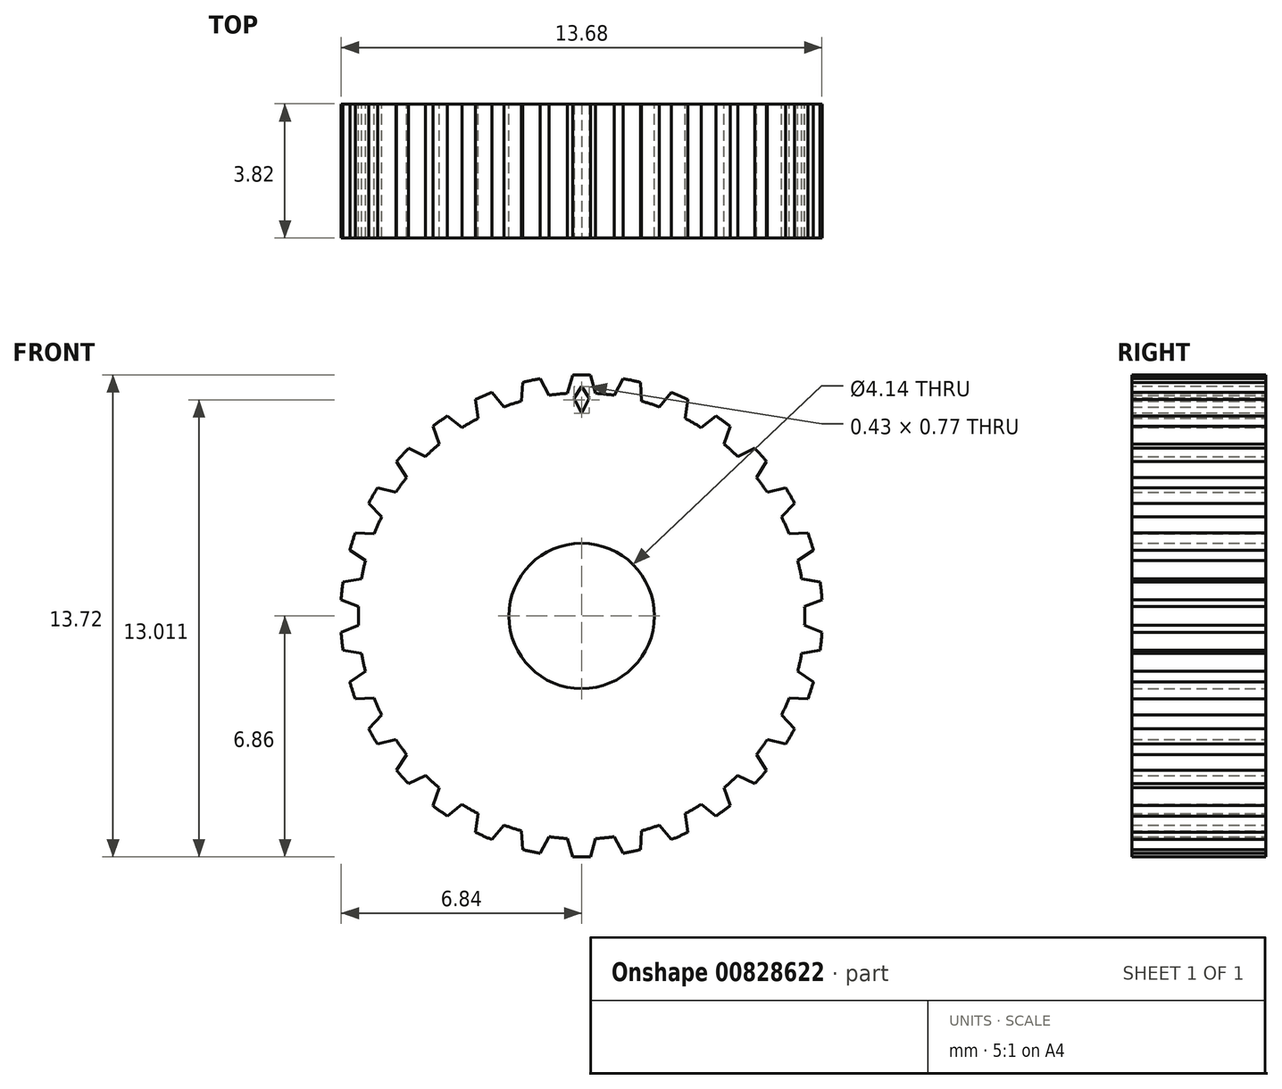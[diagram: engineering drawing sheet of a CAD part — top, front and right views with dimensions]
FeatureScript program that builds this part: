
annotation { "Feature Type Name" : "Feature", "Feature Type Description" : "" }
export const myFeature = defineFeature(function(context is Context, id is Id, definition is map)
    precondition{}
    {
        {
            var Q0;
            Q0=qCreatedBy(makeId("Front.planeOp"),FACE);
            var sketch = newSketch(context, id + "F0", { "sketchPlane" : qUnion([Q0])});
            skCircle(sketch, "E0", {"center": v(0, 0) * mm, "radius": 6.35 * mm});
            skCircle(sketch, "E1", {"center": v(0, 0) * mm, "radius": 6.86 * mm});
            skCircle(sketch, "E2", {"center": v(0, 0) * mm, "radius": 2.07 * mm});
            skLineSegment(sketch, "E3", {"start": v(-0.4, 6.34) * mm, "end": v(-0.25, 6.85) * mm});
            skLineSegment(sketch, "E4.MirrorCS", {"start": v(0.4, 6.34) * mm, "end": v(0.25, 6.85) * mm});
            skSolve(sketch);
        }
        {
            var Q0;
            {var subQ0=sQuery(id+"F0.wireOp",EDGE,"E3");Q0=makeQuery(id+"F0.imprint","IMPRINT",FACE,{"disambiguationData":[TD([[makeQuery(id+"F0.imprint","IMPRINT",EDGE,{"derivedFrom":subQ0}),-1.0]])]});}
            var Q1;
            Q1=makeQuery(id+"F0.imprint","IMPRINT",FACE,{"disambiguationData":[TD([[makeQuery(id+"F0.imprint","IMPRINT",EDGE,{"derivedFrom":sQuery(id+"F0.wireOp",EDGE,"E2")}),-1.0]])]});
            extrude(context, id + "F1", {"entities" : qUnion([Q0, Q1]), "endBound" : BoundingType.SYMMETRIC, "depth" : 3.8 * mm, "offsetDistance" : 25.4 * mm});
        }
        {
            var Q0;
            Q0=makeQuery(id+"F1.opExtrude","SWEPT_BODY",BODY,{"disambiguationData":[OSD([sQuery(id+"F0.wireOp",EDGE,"E0"),sQuery(id+"F0.wireOp",EDGE,"E1"),sQuery(id+"F0.wireOp",EDGE,"E2"),sQuery(id+"F0.wireOp",EDGE,"E3"),sQuery(id+"F0.wireOp",EDGE,"E4.MirrorCS")])]});
            var Q1;
            Q1=makeQuery(id+"F1.opExtrude","SWEPT_FACE",FACE,{"disambiguationData":[OSD([sQuery(id+"F0.wireOp",EDGE,"E4.MirrorCS")])]});
            var Q2;
            Q2=makeQuery(id+"F1.opExtrude","SWEPT_FACE",FACE,{"disambiguationData":[OSD([sQuery(id+"F0.wireOp",EDGE,"E1")])]});
            var Q3;
            Q3=makeQuery(id+"F1.opExtrude","SWEPT_FACE",FACE,{"disambiguationData":[OSD([sQuery(id+"F0.wireOp",EDGE,"E3")])]});
            var Q4;
            Q4=makeQuery(id+"F1.opExtrude","SWEPT_FACE",FACE,{"disambiguationData":[OSD([sQuery(id+"F0.wireOp",EDGE,"E0")])]});
            circularPattern(context, id + "F2", {"patternType" : PatternType.FACE, "faces" : qUnion([Q1, Q2, Q3]), "axis" : qUnion([Q4]), "angle" : 360 * degree, "instanceCount" : 30, "equalSpace" : true});
        }
        {
            var Q0;
            Q0=qCreatedBy(makeId("Front.planeOp"),FACE);
            var sketch = newSketch(context, id + "F3", { "sketchPlane" : qUnion([Q0])});
            skLineSegment(sketch, "E5", {"start": v(0, 6.54) * mm, "end": v(0, 5.77) * mm});
            skLineSegment(sketch, "E6", {"start": v(0, 5.77) * mm, "end": v(0.21, 6.2) * mm});
            skLineSegment(sketch, "E7", {"start": v(0.21, 6.2) * mm, "end": v(0, 6.54) * mm});
            skLineSegment(sketch, "E8.MirrorCS", {"start": v(-0.21, 6.2) * mm, "end": v(0, 6.54) * mm});
            skLineSegment(sketch, "E9.MirrorCS", {"start": v(0, 5.77) * mm, "end": v(-0.21, 6.2) * mm});
            skSolve(sketch);
        }
        {
            var Q0;
            Q0 = qSketchRegion(id + "F3", true);
            extrude(context, id + "F4", {"entities" : qUnion([Q0]), "operationType" : NewBodyOperationType.REMOVE, "endBound" : BoundingType.SYMMETRIC, "oppositeDirection" : true, "depth" : 25.4 * mm, "offsetDistance" : 25.4 * mm});
        }
    });
